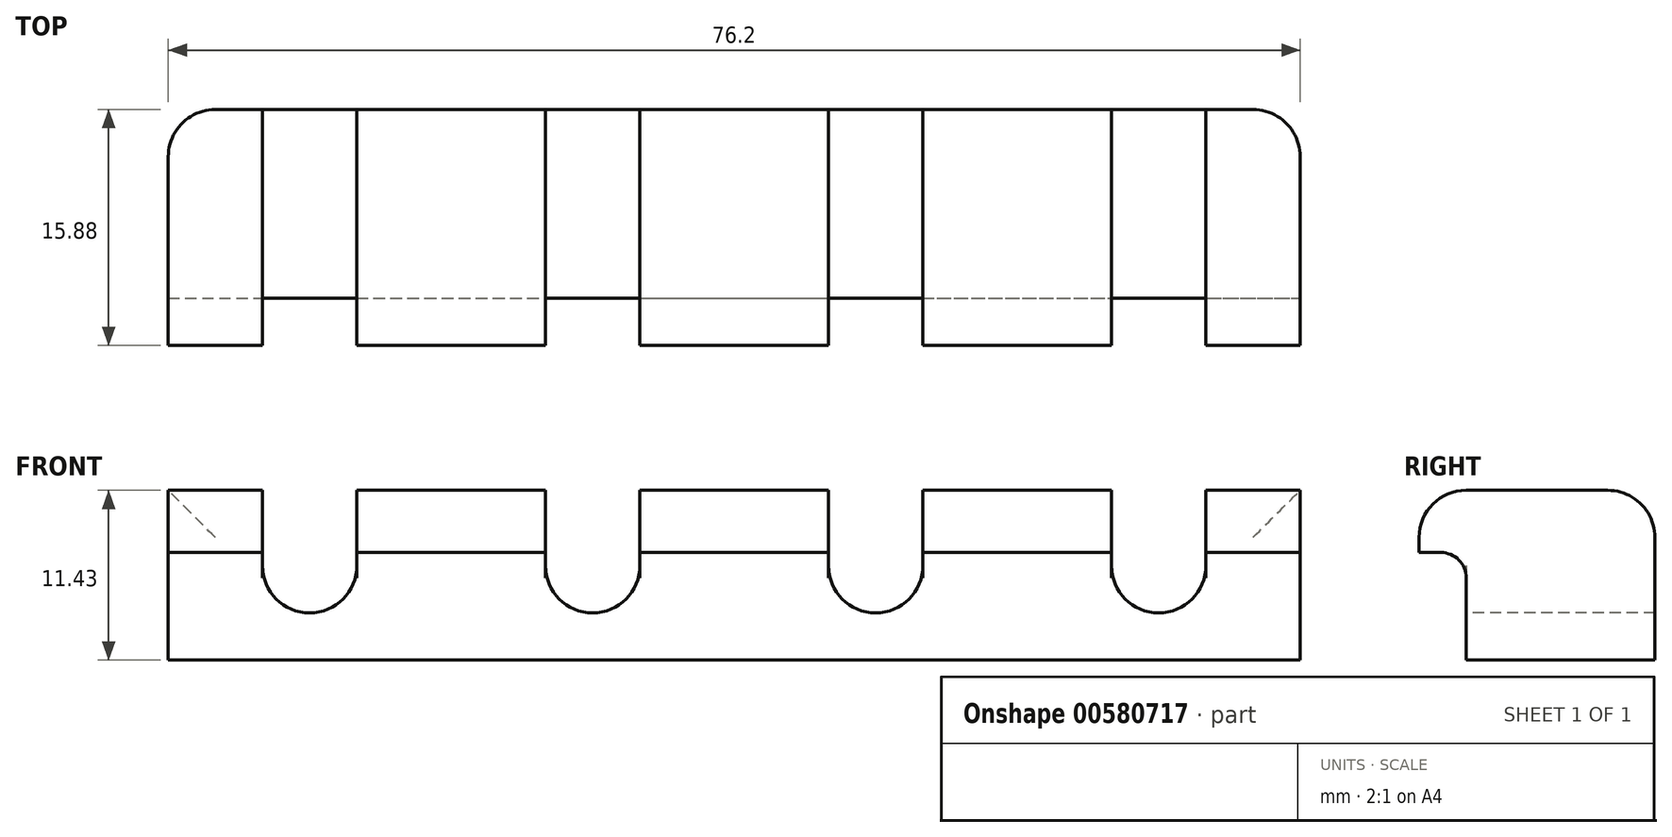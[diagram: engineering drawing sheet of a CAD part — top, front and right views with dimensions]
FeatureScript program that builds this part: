
annotation { "Feature Type Name" : "Feature", "Feature Type Description" : "" }
export const myFeature = defineFeature(function(context is Context, id is Id, definition is map)
    precondition{}
    {
        {
            var Q0;
            Q0=qCreatedBy(makeId("Top.planeOp"),FACE);
            var sketch = newSketch(context, id + "F0", { "sketchPlane" : qUnion([Q0])});
            skLineSegment(sketch, "E0.bottom", {"start": v(-50.25, 6.66) * mm, "end": v(25.95, 6.66) * mm});
            skLineSegment(sketch, "E0.top", {"start": v(-50.25, -6.04) * mm, "end": v(25.95, -6.04) * mm});
            skLineSegment(sketch, "E0.left", {"start": v(-50.25, 6.66) * mm, "end": v(-50.25, -6.04) * mm});
            skLineSegment(sketch, "E0.right", {"start": v(25.95, 6.66) * mm, "end": v(25.95, -6.04) * mm});
            skSolve(sketch);
        }
        {
            var Q0;
            Q0 = qSketchRegion(id + "F0", true);
            extrude(context, id + "F1", {"entities" : qUnion([Q0]), "depth" : 3.17 * mm, "offsetDistance" : 25.4 * mm});
        }
        {
            var Q0;
            Q0=makeQuery(id+"F1.opExtrude","CAP_FACE",FACE,{"disambiguationData":[OSD([sQuery(id+"F0.wireOp",EDGE,"E0.bottom"),sQuery(id+"F0.wireOp",EDGE,"E0.top"),sQuery(id+"F0.wireOp",EDGE,"E0.left"),sQuery(id+"F0.wireOp",EDGE,"E0.right")])],"isStart":false});
            var sketch = newSketch(context, id + "F2", { "sketchPlane" : qUnion([Q0])});
            skLineSegment(sketch, "E1.bottom", {"start": v(-50.25, 6.66) * mm, "end": v(-43.9, 6.66) * mm});
            skLineSegment(sketch, "E1.top", {"start": v(-50.25, -6.04) * mm, "end": v(-43.9, -6.04) * mm});
            skLineSegment(sketch, "E1.left", {"start": v(-50.25, 6.66) * mm, "end": v(-50.25, -6.04) * mm});
            skLineSegment(sketch, "E1.right", {"start": v(-43.9, 6.66) * mm, "end": v(-43.9, -6.04) * mm});
            skLineSegment(sketch, "E2.bottom", {"start": v(-37.55, 6.66) * mm, "end": v(-24.85, 6.66) * mm});
            skLineSegment(sketch, "E2.top", {"start": v(-37.55, -6.04) * mm, "end": v(-24.85, -6.04) * mm});
            skLineSegment(sketch, "E2.left", {"start": v(-37.55, 6.66) * mm, "end": v(-37.55, -6.04) * mm});
            skLineSegment(sketch, "E2.right", {"start": v(-24.85, 6.66) * mm, "end": v(-24.85, -6.04) * mm});
            skLineSegment(sketch, "E3.bottom", {"start": v(-18.5, 6.66) * mm, "end": v(-5.8, 6.66) * mm});
            skLineSegment(sketch, "E3.top", {"start": v(-18.5, -6.04) * mm, "end": v(-5.8, -6.04) * mm});
            skLineSegment(sketch, "E3.left", {"start": v(-18.5, 6.66) * mm, "end": v(-18.5, -6.04) * mm});
            skLineSegment(sketch, "E3.right", {"start": v(-5.8, 6.66) * mm, "end": v(-5.8, -6.04) * mm});
            skLineSegment(sketch, "E4.bottom", {"start": v(0.55, 6.66) * mm, "end": v(13.25, 6.66) * mm});
            skLineSegment(sketch, "E4.top", {"start": v(0.55, -6.04) * mm, "end": v(13.25, -6.04) * mm});
            skLineSegment(sketch, "E4.left", {"start": v(0.55, 6.66) * mm, "end": v(0.55, -6.04) * mm});
            skLineSegment(sketch, "E4.right", {"start": v(13.25, 6.66) * mm, "end": v(13.25, -6.04) * mm});
            skLineSegment(sketch, "E5.bottom", {"start": v(25.95, 6.66) * mm, "end": v(19.6, 6.66) * mm});
            skLineSegment(sketch, "E5.top", {"start": v(25.95, -6.04) * mm, "end": v(19.6, -6.04) * mm});
            skLineSegment(sketch, "E5.left", {"start": v(25.95, 6.66) * mm, "end": v(25.95, -6.04) * mm});
            skLineSegment(sketch, "E5.right", {"start": v(19.6, 6.66) * mm, "end": v(19.6, -6.04) * mm});
            skSolve(sketch);
        }
        {
            var Q0;
            Q0=makeQuery(id+"F2.imprint","IMPRINT",FACE,{"disambiguationData":[TD([[makeQuery(id+"F2.imprint","IMPRINT",EDGE,{"derivedFrom":sQuery(id+"F2.wireOp",EDGE,"E1.bottom")}),-1.0]])]});
            var Q1;
            Q1=makeQuery(id+"F2.imprint","IMPRINT",FACE,{"disambiguationData":[TD([[makeQuery(id+"F2.imprint","IMPRINT",EDGE,{"derivedFrom":sQuery(id+"F2.wireOp",EDGE,"E2.bottom")}),-1.0]])]});
            var Q2;
            Q2=makeQuery(id+"F2.imprint","IMPRINT",FACE,{"disambiguationData":[TD([[makeQuery(id+"F2.imprint","IMPRINT",EDGE,{"derivedFrom":sQuery(id+"F2.wireOp",EDGE,"E3.bottom")}),-1.0]])]});
            var Q3;
            Q3=makeQuery(id+"F2.imprint","IMPRINT",FACE,{"disambiguationData":[TD([[makeQuery(id+"F2.imprint","IMPRINT",EDGE,{"derivedFrom":sQuery(id+"F2.wireOp",EDGE,"E4.bottom")}),-1.0]])]});
            var Q4;
            Q4=makeQuery(id+"F2.imprint","IMPRINT",FACE,{"disambiguationData":[TD([[makeQuery(id+"F2.imprint","IMPRINT",EDGE,{"derivedFrom":sQuery(id+"F2.wireOp",EDGE,"E5.bottom")}),-1.0]])]});
            extrude(context, id + "F3", {"entities" : qUnion([Q0, Q1, Q2, Q3, Q4]), "operationType" : NewBodyOperationType.ADD, "depth" : 8.25 * mm, "offsetDistance" : 25.4 * mm});
        }
        {
            var Q0;
            Q0=makeQuery(id+"F3.boolean.opBoolean","MERGE",FACE,{"derivedFrom":[makeQuery(id+"F1.opExtrude","SWEPT_FACE",FACE,{"disambiguationData":[OSD([sQuery(id+"F0.wireOp",EDGE,"E0.top")])]}),makeQuery(id+"F3.opExtrude","SWEPT_FACE",FACE,{"disambiguationData":[OSD([sQuery(id+"F2.wireOp",EDGE,"E1.top")])]}),makeQuery(id+"F3.opExtrude","SWEPT_FACE",FACE,{"disambiguationData":[OSD([sQuery(id+"F2.wireOp",EDGE,"E2.top")])]}),makeQuery(id+"F3.opExtrude","SWEPT_FACE",FACE,{"disambiguationData":[OSD([sQuery(id+"F2.wireOp",EDGE,"E3.top")])]}),makeQuery(id+"F3.opExtrude","SWEPT_FACE",FACE,{"disambiguationData":[OSD([sQuery(id+"F2.wireOp",EDGE,"E4.top")])]}),makeQuery(id+"F3.opExtrude","SWEPT_FACE",FACE,{"disambiguationData":[OSD([sQuery(id+"F2.wireOp",EDGE,"E5.top")])]})]});
            var sketch = newSketch(context, id + "F4", { "sketchPlane" : qUnion([Q0])});
            skLineSegment(sketch, "E6.bottom", {"start": v(-50.25, 11.43) * mm, "end": v(-43.9, 11.43) * mm});
            skLineSegment(sketch, "E6.top", {"start": v(-50.25, 7.24) * mm, "end": v(-43.9, 7.24) * mm});
            skLineSegment(sketch, "E6.left", {"start": v(-50.25, 11.43) * mm, "end": v(-50.25, 7.24) * mm});
            skLineSegment(sketch, "E6.right", {"start": v(-43.9, 11.43) * mm, "end": v(-43.9, 7.24) * mm});
            skLineSegment(sketch, "E7.bottom", {"start": v(-37.55, 11.43) * mm, "end": v(-24.85, 11.43) * mm});
            skLineSegment(sketch, "E7.top", {"start": v(-37.55, 7.24) * mm, "end": v(-24.85, 7.24) * mm});
            skLineSegment(sketch, "E7.left", {"start": v(-37.55, 11.43) * mm, "end": v(-37.55, 7.24) * mm});
            skLineSegment(sketch, "E7.right", {"start": v(-24.85, 11.43) * mm, "end": v(-24.85, 7.24) * mm});
            skLineSegment(sketch, "E8.bottom", {"start": v(-18.5, 11.43) * mm, "end": v(-5.8, 11.43) * mm});
            skLineSegment(sketch, "E8.top", {"start": v(-18.5, 7.24) * mm, "end": v(-5.8, 7.24) * mm});
            skLineSegment(sketch, "E8.left", {"start": v(-18.5, 11.43) * mm, "end": v(-18.5, 7.24) * mm});
            skLineSegment(sketch, "E8.right", {"start": v(-5.8, 11.43) * mm, "end": v(-5.8, 7.24) * mm});
            skLineSegment(sketch, "E9.bottom", {"start": v(0.55, 11.43) * mm, "end": v(13.25, 11.43) * mm});
            skLineSegment(sketch, "E9.top", {"start": v(0.55, 7.24) * mm, "end": v(13.25, 7.24) * mm});
            skLineSegment(sketch, "E9.left", {"start": v(0.55, 11.43) * mm, "end": v(0.55, 7.24) * mm});
            skLineSegment(sketch, "E9.right", {"start": v(13.25, 11.43) * mm, "end": v(13.25, 7.24) * mm});
            skLineSegment(sketch, "E10.bottom", {"start": v(19.6, 11.43) * mm, "end": v(25.95, 11.43) * mm});
            skLineSegment(sketch, "E10.top", {"start": v(19.6, 7.24) * mm, "end": v(25.95, 7.24) * mm});
            skLineSegment(sketch, "E10.left", {"start": v(19.6, 11.43) * mm, "end": v(19.6, 7.24) * mm});
            skLineSegment(sketch, "E10.right", {"start": v(25.95, 11.43) * mm, "end": v(25.95, 7.24) * mm});
            skSolve(sketch);
        }
        {
            var Q0;
            Q0 = qSketchRegion(id + "F4", true);
            extrude(context, id + "F5", {"entities" : qUnion([Q0]), "operationType" : NewBodyOperationType.ADD, "depth" : 3.17 * mm, "offsetDistance" : 25.4 * mm});
        }
        {
            var Q0;
            Q0=makeQuery(id+"F5.boolean.opBoolean","MERGE",FACE,{"derivedFrom":[makeQuery(id+"F3.boolean.opBoolean","MERGE",FACE,{"derivedFrom":[makeQuery(id+"F1.opExtrude","SWEPT_FACE",FACE,{"disambiguationData":[OSD([sQuery(id+"F0.wireOp",EDGE,"E0.right")])]}),makeQuery(id+"F3.opExtrude","SWEPT_FACE",FACE,{"disambiguationData":[OSD([sQuery(id+"F2.wireOp",EDGE,"E5.left")])]})]}),makeQuery(id+"F5.opExtrude","SWEPT_FACE",FACE,{"disambiguationData":[OSD([sQuery(id+"F4.wireOp",EDGE,"E10.right")])]})]});
            var sketch = newSketch(context, id + "F6", { "sketchPlane" : qUnion([Q0])});
            skLineSegment(sketch, "E11", {"start": v(-9.22, 7.24) * mm, "end": v(-7.76, 7.24) * mm});
            skLineSegment(sketch, "E12", {"start": v(-6.04, 5.52) * mm, "end": v(-6.04, 0) * mm});
            skPoint(sketch, "E13.visualSharp", {"position": v(-6.04, 7.24) * mm});
            skArc(sketch, "E13.filletArc", {"start": v(-6.04, 5.52) * mm, "mid": v(-6.54, 6.74) * mm, "end": v(-7.76, 7.24) * mm});
            skSolve(sketch);
        }
        {
            var Q0;
            {var subQ0=sQuery(id+"F6.wireOp",EDGE,"E13.filletArc");Q0=makeQuery(id+"F6.imprint","IMPRINT",FACE,{"disambiguationData":[TD([[makeQuery(id+"F6.imprint","IMPRINT",EDGE,{"derivedFrom":subQ0}),-1.0]])]});}
            extrude(context, id + "F7", {"entities" : qUnion([Q0]), "operationType" : NewBodyOperationType.ADD, "oppositeDirection" : true, "depth" : 6.35 * mm, "offsetDistance" : 25.4 * mm});
        }
        {
            var Q0;
            Q0=makeQuery(id+"F5.boolean.opBoolean","MERGE",FACE,{"derivedFrom":[makeQuery(id+"F3.opExtrude","SWEPT_FACE",FACE,{"disambiguationData":[OSD([sQuery(id+"F2.wireOp",EDGE,"E4.right")])]}),makeQuery(id+"F5.opExtrude","SWEPT_FACE",FACE,{"disambiguationData":[OSD([sQuery(id+"F4.wireOp",EDGE,"E9.right")])]})]});
            var sketch = newSketch(context, id + "F8", { "sketchPlane" : qUnion([Q0])});
            skLineSegment(sketch, "E14", {"start": v(-9.22, 7.24) * mm, "end": v(-7.76, 7.24) * mm});
            skLineSegment(sketch, "E15", {"start": v(-6.04, 5.52) * mm, "end": v(-6.04, 3.18) * mm});
            skPoint(sketch, "E16.visualSharp", {"position": v(-6.04, 7.24) * mm});
            skArc(sketch, "E16.filletArc", {"start": v(-6.04, 5.52) * mm, "mid": v(-6.54, 6.74) * mm, "end": v(-7.76, 7.24) * mm});
            skSolve(sketch);
        }
        {
            var Q0;
            {var subQ0=sQuery(id+"F8.wireOp",EDGE,"E16.filletArc");Q0=makeQuery(id+"F8.imprint","IMPRINT",FACE,{"disambiguationData":[TD([[makeQuery(id+"F8.imprint","IMPRINT",EDGE,{"derivedFrom":subQ0}),-1.0]])]});}
            extrude(context, id + "F9", {"entities" : qUnion([Q0]), "operationType" : NewBodyOperationType.ADD, "oppositeDirection" : true, "depth" : 12.7 * mm, "offsetDistance" : 25.4 * mm});
        }
        {
            var Q0;
            Q0=makeQuery(id+"F5.boolean.opBoolean","MERGE",FACE,{"derivedFrom":[makeQuery(id+"F3.opExtrude","SWEPT_FACE",FACE,{"disambiguationData":[OSD([sQuery(id+"F2.wireOp",EDGE,"E3.right")])]}),makeQuery(id+"F5.opExtrude","SWEPT_FACE",FACE,{"disambiguationData":[OSD([sQuery(id+"F4.wireOp",EDGE,"E8.right")])]})]});
            var sketch = newSketch(context, id + "F10", { "sketchPlane" : qUnion([Q0])});
            skLineSegment(sketch, "E17", {"start": v(-9.22, 7.24) * mm, "end": v(-7.76, 7.24) * mm});
            skLineSegment(sketch, "E18", {"start": v(-6.04, 5.52) * mm, "end": v(-6.04, 3.18) * mm});
            skPoint(sketch, "E19.visualSharp", {"position": v(-6.04, 7.24) * mm});
            skArc(sketch, "E19.filletArc", {"start": v(-6.04, 5.52) * mm, "mid": v(-6.54, 6.74) * mm, "end": v(-7.76, 7.24) * mm});
            skSolve(sketch);
        }
        {
            var Q0;
            {var subQ0=sQuery(id+"F10.wireOp",EDGE,"E19.filletArc");Q0=makeQuery(id+"F10.imprint","IMPRINT",FACE,{"disambiguationData":[TD([[makeQuery(id+"F10.imprint","IMPRINT",EDGE,{"derivedFrom":subQ0}),-1.0]])]});}
            extrude(context, id + "F11", {"entities" : qUnion([Q0]), "operationType" : NewBodyOperationType.ADD, "oppositeDirection" : true, "depth" : 12.7 * mm, "offsetDistance" : 25.4 * mm});
        }
        {
            var Q0;
            Q0=makeQuery(id+"F5.boolean.opBoolean","MERGE",FACE,{"derivedFrom":[makeQuery(id+"F3.opExtrude","SWEPT_FACE",FACE,{"disambiguationData":[OSD([sQuery(id+"F2.wireOp",EDGE,"E2.right")])]}),makeQuery(id+"F5.opExtrude","SWEPT_FACE",FACE,{"disambiguationData":[OSD([sQuery(id+"F4.wireOp",EDGE,"E7.right")])]})]});
            var sketch = newSketch(context, id + "F12", { "sketchPlane" : qUnion([Q0])});
            skLineSegment(sketch, "E20", {"start": v(-9.22, 7.24) * mm, "end": v(-7.76, 7.24) * mm});
            skLineSegment(sketch, "E21", {"start": v(-6.04, 5.52) * mm, "end": v(-6.04, 3.18) * mm});
            skPoint(sketch, "E22.visualSharp", {"position": v(-6.04, 7.24) * mm});
            skArc(sketch, "E22.filletArc", {"start": v(-6.04, 5.52) * mm, "mid": v(-6.54, 6.74) * mm, "end": v(-7.76, 7.24) * mm});
            skSolve(sketch);
        }
        {
            var Q0;
            {var subQ0=sQuery(id+"F12.wireOp",EDGE,"E22.filletArc");Q0=makeQuery(id+"F12.imprint","IMPRINT",FACE,{"disambiguationData":[TD([[makeQuery(id+"F12.imprint","IMPRINT",EDGE,{"derivedFrom":subQ0}),-1.0]])]});}
            extrude(context, id + "F13", {"entities" : qUnion([Q0]), "operationType" : NewBodyOperationType.ADD, "oppositeDirection" : true, "depth" : 12.7 * mm, "offsetDistance" : 25.4 * mm});
        }
        {
            var Q0;
            Q0=makeQuery(id+"F5.boolean.opBoolean","MERGE",FACE,{"derivedFrom":[makeQuery(id+"F3.opExtrude","SWEPT_FACE",FACE,{"disambiguationData":[OSD([sQuery(id+"F2.wireOp",EDGE,"E1.right")])]}),makeQuery(id+"F5.opExtrude","SWEPT_FACE",FACE,{"disambiguationData":[OSD([sQuery(id+"F4.wireOp",EDGE,"E6.right")])]})]});
            var sketch = newSketch(context, id + "F14", { "sketchPlane" : qUnion([Q0])});
            skLineSegment(sketch, "E23", {"start": v(-9.22, 7.24) * mm, "end": v(-7.76, 7.24) * mm});
            skLineSegment(sketch, "E24", {"start": v(-6.04, 5.52) * mm, "end": v(-6.04, 3.18) * mm});
            skPoint(sketch, "E25.visualSharp", {"position": v(-6.04, 7.24) * mm});
            skArc(sketch, "E25.filletArc", {"start": v(-6.04, 5.52) * mm, "mid": v(-6.54, 6.74) * mm, "end": v(-7.76, 7.24) * mm});
            skSolve(sketch);
        }
        {
            var Q0;
            {var subQ0=sQuery(id+"F14.wireOp",EDGE,"E25.filletArc");Q0=makeQuery(id+"F14.imprint","IMPRINT",FACE,{"disambiguationData":[TD([[makeQuery(id+"F14.imprint","IMPRINT",EDGE,{"derivedFrom":subQ0}),-1.0]])]});}
            extrude(context, id + "F15", {"entities" : qUnion([Q0]), "operationType" : NewBodyOperationType.ADD, "oppositeDirection" : true, "depth" : 6.35 * mm, "offsetDistance" : 25.4 * mm});
        }
        {
            var Q0;
            Q0=makeQuery(id+"F3.boolean.opBoolean","MERGE",FACE,{"derivedFrom":[makeQuery(id+"F1.opExtrude","SWEPT_FACE",FACE,{"disambiguationData":[OSD([sQuery(id+"F0.wireOp",EDGE,"E0.top")])]}),makeQuery(id+"F3.opExtrude","SWEPT_FACE",FACE,{"disambiguationData":[OSD([sQuery(id+"F2.wireOp",EDGE,"E1.top")])]}),makeQuery(id+"F3.opExtrude","SWEPT_FACE",FACE,{"disambiguationData":[OSD([sQuery(id+"F2.wireOp",EDGE,"E2.top")])]}),makeQuery(id+"F3.opExtrude","SWEPT_FACE",FACE,{"disambiguationData":[OSD([sQuery(id+"F2.wireOp",EDGE,"E3.top")])]}),makeQuery(id+"F3.opExtrude","SWEPT_FACE",FACE,{"disambiguationData":[OSD([sQuery(id+"F2.wireOp",EDGE,"E4.top")])]}),makeQuery(id+"F3.opExtrude","SWEPT_FACE",FACE,{"disambiguationData":[OSD([sQuery(id+"F2.wireOp",EDGE,"E5.top")])]})]});
            var sketch = newSketch(context, id + "F16", { "sketchPlane" : qUnion([Q0])});
            skLineSegment(sketch, "E26", {"start": v(-43.9, 6.35) * mm, "end": v(-43.9, 5.52) * mm});
            skLineSegment(sketch, "E27", {"start": v(-40.73, 3.18) * mm, "end": v(-40.73, 3.18) * mm});
            skLineSegment(sketch, "E28", {"start": v(-37.55, 5.52) * mm, "end": v(-37.55, 6.35) * mm});
            skLineSegment(sketch, "E29", {"start": v(-37.55, 5.52) * mm, "end": v(-24.85, 5.52) * mm});
            skLineSegment(sketch, "E30", {"start": v(-24.85, 6.35) * mm, "end": v(-24.85, 5.52) * mm});
            skLineSegment(sketch, "E31", {"start": v(-21.68, 3.18) * mm, "end": v(-21.68, 3.18) * mm});
            skLineSegment(sketch, "E32", {"start": v(-18.5, 5.52) * mm, "end": v(-18.5, 6.35) * mm});
            skLineSegment(sketch, "E33", {"start": v(-18.5, 5.52) * mm, "end": v(-5.8, 5.52) * mm});
            skLineSegment(sketch, "E34", {"start": v(-5.8, 6.35) * mm, "end": v(-5.8, 5.52) * mm});
            skLineSegment(sketch, "E35", {"start": v(-2.63, 3.18) * mm, "end": v(-2.63, 3.18) * mm});
            skLineSegment(sketch, "E36", {"start": v(0.55, 5.52) * mm, "end": v(0.55, 6.35) * mm});
            skLineSegment(sketch, "E37", {"start": v(0.55, 5.52) * mm, "end": v(13.25, 5.52) * mm});
            skLineSegment(sketch, "E38", {"start": v(13.25, 6.35) * mm, "end": v(13.25, 5.52) * mm});
            skLineSegment(sketch, "E39", {"start": v(16.42, 3.18) * mm, "end": v(16.42, 3.18) * mm});
            skLineSegment(sketch, "E40", {"start": v(19.6, 5.52) * mm, "end": v(19.6, 6.35) * mm});
            skPoint(sketch, "E41.visualSharp", {"position": v(19.6, 3.18) * mm});
            skArc(sketch, "E41.filletArc", {"start": v(16.42, 3.18) * mm, "mid": v(18.67, 4.1) * mm, "end": v(19.6, 6.35) * mm});
            skPoint(sketch, "E42.visualSharp", {"position": v(13.25, 3.18) * mm});
            skArc(sketch, "E42.filletArc", {"start": v(13.25, 6.35) * mm, "mid": v(14.18, 4.1) * mm, "end": v(16.42, 3.18) * mm});
            skPoint(sketch, "E43.visualSharp", {"position": v(0.55, 3.18) * mm});
            skArc(sketch, "E43.filletArc", {"start": v(-2.63, 3.18) * mm, "mid": v(-0.38, 4.1) * mm, "end": v(0.55, 6.35) * mm});
            skPoint(sketch, "E44.visualSharp", {"position": v(-5.8, 3.18) * mm});
            skArc(sketch, "E44.filletArc", {"start": v(-5.8, 6.35) * mm, "mid": v(-4.87, 4.1) * mm, "end": v(-2.63, 3.18) * mm});
            skPoint(sketch, "E45.visualSharp", {"position": v(-24.85, 3.18) * mm});
            skArc(sketch, "E45.filletArc", {"start": v(-24.85, 6.35) * mm, "mid": v(-23.92, 4.1) * mm, "end": v(-21.68, 3.18) * mm});
            skPoint(sketch, "E46.visualSharp", {"position": v(-18.5, 3.18) * mm});
            skArc(sketch, "E46.filletArc", {"start": v(-21.68, 3.18) * mm, "mid": v(-19.43, 4.1) * mm, "end": v(-18.5, 6.35) * mm});
            skPoint(sketch, "E47.visualSharp", {"position": v(-43.9, 3.18) * mm});
            skArc(sketch, "E47.filletArc", {"start": v(-43.9, 6.35) * mm, "mid": v(-42.97, 4.1) * mm, "end": v(-40.73, 3.18) * mm});
            skPoint(sketch, "E48.visualSharp", {"position": v(-37.55, 3.18) * mm});
            skArc(sketch, "E48.filletArc", {"start": v(-40.73, 3.18) * mm, "mid": v(-38.48, 4.1) * mm, "end": v(-37.55, 6.35) * mm});
            skSolve(sketch);
        }
        {
            var Q0;
            Q0=makeQuery(id+"F16.imprint","IMPRINT",FACE,{"disambiguationData":[TD([[makeQuery(id+"F16.imprint","IMPRINT",EDGE,{"derivedFrom":sQuery(id+"F16.wireOp",EDGE,"E26")}),1.0]])]});
            var Q1;
            Q1=makeQuery(id+"F16.imprint","IMPRINT",FACE,{"disambiguationData":[TD([[makeQuery(id+"F16.imprint","IMPRINT",EDGE,{"derivedFrom":sQuery(id+"F16.wireOp",EDGE,"E28")}),1.0]])]});
            var Q2;
            Q2=makeQuery(id+"F16.imprint","IMPRINT",FACE,{"disambiguationData":[TD([[makeQuery(id+"F16.imprint","IMPRINT",EDGE,{"derivedFrom":sQuery(id+"F16.wireOp",EDGE,"E30")}),1.0]])]});
            var Q3;
            Q3=makeQuery(id+"F16.imprint","IMPRINT",FACE,{"disambiguationData":[TD([[makeQuery(id+"F16.imprint","IMPRINT",EDGE,{"derivedFrom":sQuery(id+"F16.wireOp",EDGE,"E32")}),1.0]])]});
            var Q4;
            Q4=makeQuery(id+"F16.imprint","IMPRINT",FACE,{"disambiguationData":[TD([[makeQuery(id+"F16.imprint","IMPRINT",EDGE,{"derivedFrom":sQuery(id+"F16.wireOp",EDGE,"E34")}),1.0]])]});
            var Q5;
            Q5=makeQuery(id+"F16.imprint","IMPRINT",FACE,{"disambiguationData":[TD([[makeQuery(id+"F16.imprint","IMPRINT",EDGE,{"derivedFrom":sQuery(id+"F16.wireOp",EDGE,"E36")}),1.0]])]});
            var Q6;
            Q6=makeQuery(id+"F16.imprint","IMPRINT",FACE,{"disambiguationData":[TD([[makeQuery(id+"F16.imprint","IMPRINT",EDGE,{"derivedFrom":sQuery(id+"F16.wireOp",EDGE,"E38")}),1.0]])]});
            var Q7;
            Q7=makeQuery(id+"F16.imprint","IMPRINT",FACE,{"disambiguationData":[TD([[makeQuery(id+"F16.imprint","IMPRINT",EDGE,{"derivedFrom":sQuery(id+"F16.wireOp",EDGE,"E40")}),1.0]])]});
            extrude(context, id + "F17", {"entities" : qUnion([Q0, Q1, Q2, Q3, Q4, Q5, Q6, Q7]), "operationType" : NewBodyOperationType.ADD, "oppositeDirection" : true, "depth" : 12.7 * mm, "offsetDistance" : 25.4 * mm});
        }
        {
            var Q0;
            Q0=makeQuery(id+"F3.opExtrude","CAP_EDGE",EDGE,{"disambiguationData":[OSD([sQuery(id+"F2.wireOp",EDGE,"E5.bottom")])],"isStart":false});
            var Q1;
            Q1=makeQuery(id+"F3.opExtrude","CAP_EDGE",EDGE,{"disambiguationData":[OSD([sQuery(id+"F2.wireOp",EDGE,"E4.bottom")])],"isStart":false});
            var Q2;
            Q2=makeQuery(id+"F3.opExtrude","CAP_EDGE",EDGE,{"disambiguationData":[OSD([sQuery(id+"F2.wireOp",EDGE,"E3.bottom")])],"isStart":false});
            var Q3;
            Q3=makeQuery(id+"F3.opExtrude","CAP_EDGE",EDGE,{"disambiguationData":[OSD([sQuery(id+"F2.wireOp",EDGE,"E2.bottom")])],"isStart":false});
            var Q4;
            Q4=makeQuery(id+"F3.opExtrude","CAP_EDGE",EDGE,{"disambiguationData":[OSD([sQuery(id+"F2.wireOp",EDGE,"E1.bottom")])],"isStart":false});
            var Q5;
            Q5=makeQuery(id+"F5.opExtrude","CAP_EDGE",EDGE,{"disambiguationData":[OSD([sQuery(id+"F4.wireOp",EDGE,"E6.bottom")])],"isStart":false});
            var Q6;
            Q6=makeQuery(id+"F5.opExtrude","CAP_EDGE",EDGE,{"disambiguationData":[OSD([sQuery(id+"F4.wireOp",EDGE,"E7.bottom")])],"isStart":false});
            var Q7;
            Q7=makeQuery(id+"F5.opExtrude","CAP_EDGE",EDGE,{"disambiguationData":[OSD([sQuery(id+"F4.wireOp",EDGE,"E8.bottom")])],"isStart":false});
            var Q8;
            Q8=makeQuery(id+"F5.opExtrude","CAP_EDGE",EDGE,{"disambiguationData":[OSD([sQuery(id+"F4.wireOp",EDGE,"E9.bottom")])],"isStart":false});
            var Q9;
            Q9=makeQuery(id+"F5.opExtrude","CAP_EDGE",EDGE,{"disambiguationData":[OSD([sQuery(id+"F4.wireOp",EDGE,"E10.bottom")])],"isStart":false});
            var Q10;
            Q10=makeQuery(id+"F3.boolean.opBoolean","MERGE",EDGE,{"derivedFrom":[makeQuery(id+"F1.opExtrude","SWEPT_EDGE",EDGE,{"disambiguationData":[OSD([sQuery(id+"F0.wireOp",EDGE,"E0.bottom"),sQuery(id+"F0.wireOp",EDGE,"E0.left")])]}),makeQuery(id+"F3.opExtrude","SWEPT_EDGE",EDGE,{"disambiguationData":[OSD([sQuery(id+"F2.wireOp",EDGE,"E1.bottom"),sQuery(id+"F2.wireOp",EDGE,"E1.left")])]})]});
            var Q11;
            Q11=makeQuery(id+"F3.boolean.opBoolean","MERGE",EDGE,{"derivedFrom":[makeQuery(id+"F1.opExtrude","SWEPT_EDGE",EDGE,{"disambiguationData":[OSD([sQuery(id+"F0.wireOp",EDGE,"E0.bottom"),sQuery(id+"F0.wireOp",EDGE,"E0.right")])]}),makeQuery(id+"F3.opExtrude","SWEPT_EDGE",EDGE,{"disambiguationData":[OSD([sQuery(id+"F2.wireOp",EDGE,"E5.bottom"),sQuery(id+"F2.wireOp",EDGE,"E5.left")])]})]});
            fillet(context, id + "F18", {"entities" : qUnion([Q0, Q1, Q2, Q3, Q4, Q5, Q6, Q7, Q8, Q9, Q10, Q11]), "radius" : 3.17 * mm, "tangentPropagation" : true, "allowEdgeOverflow" : false});
        }
    });
